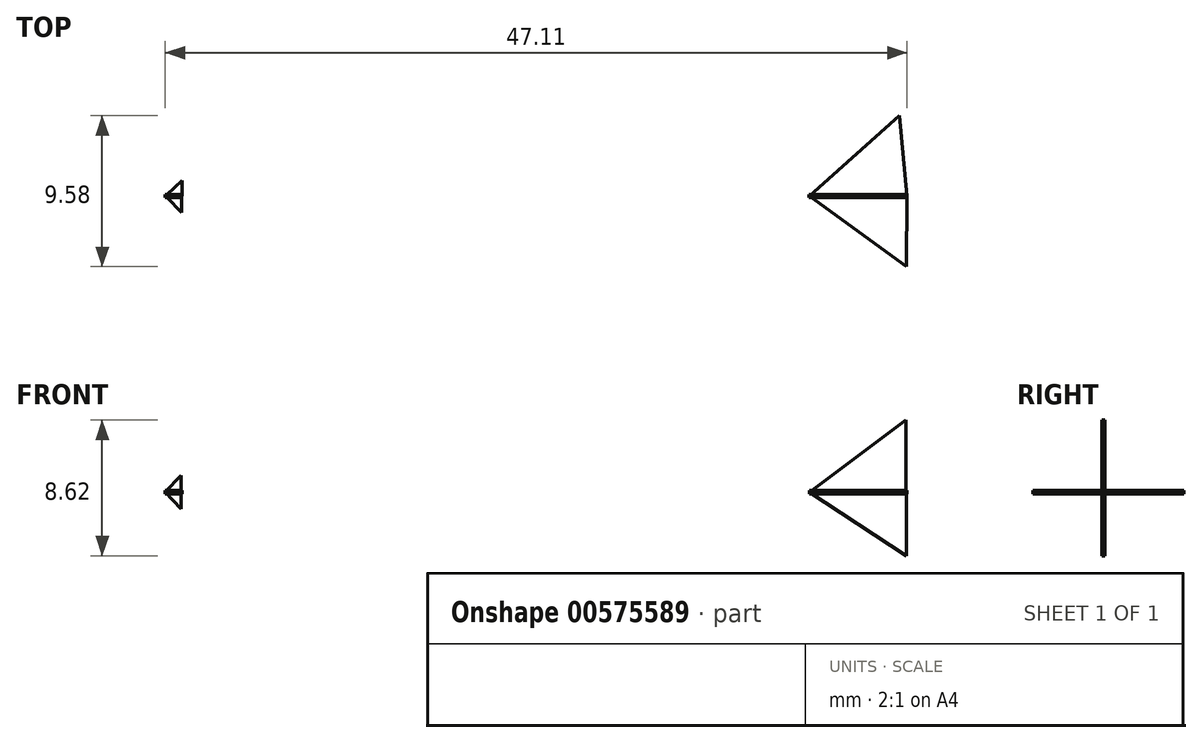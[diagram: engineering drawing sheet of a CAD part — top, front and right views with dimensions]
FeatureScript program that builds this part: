
annotation { "Feature Type Name" : "Feature", "Feature Type Description" : "" }
export const myFeature = defineFeature(function(context is Context, id is Id, definition is map)
    precondition{}
    {
        {
            var Q0;
            Q0=qCreatedBy(makeId("Front.planeOp"),FACE);
            var sketch = newSketch(context, id + "F0", { "sketchPlane" : qUnion([Q0])});
            skLineSegment(sketch, "E0", {"start": v(0, 67.82) * mm, "end": v(0, -67.31) * mm});
            skArc(sketch, "E1", {"start": v(0, 67.82) * mm, "mid": v(-28.44, 0.25) * mm, "end": v(0, -67.31) * mm});
            skSolve(sketch);
        }
        {
            var Q0;
            Q0=sQuery(id+"F0.wireOp",EDGE,"E1");
            extrude(context, id + "F1", {"bodyType" : ToolBodyType.SURFACE, "surfaceEntities" : qUnion([Q0]), "endBound" : BoundingType.SYMMETRIC, "depth" : 2.54 * mm, "offsetDistance" : 25.4 * mm});
        }
        {
            var Q0;
            Q0=qCreatedBy(makeId("Front.planeOp"),FACE);
            var sketch = newSketch(context, id + "F2", { "sketchPlane" : qUnion([Q0])});
            skLineSegment(sketch, "E2", {"start": v(-39.36, 0) * mm, "end": v(7.7, 0) * mm});
            skLineSegment(sketch, "E3", {"start": v(7.7, 0) * mm, "end": v(7.7, 4.58) * mm});
            skLineSegment(sketch, "E4", {"start": v(7.7, 4.58) * mm, "end": v(1.58, 0) * mm});
            skLineSegment(sketch, "E5", {"start": v(1.58, 0) * mm, "end": v(7.7, -4.6) * mm});
            skLineSegment(sketch, "E6", {"start": v(7.74, -4.6) * mm, "end": v(7.7, 0) * mm});
            skLineSegment(sketch, "E7", {"start": v(-39.36, 0) * mm, "end": v(-38.35, 1.07) * mm});
            skLineSegment(sketch, "E8", {"start": v(-38.35, 1.07) * mm, "end": v(-38.35, 0) * mm});
            skLineSegment(sketch, "E9", {"start": v(-38.35, 0) * mm, "end": v(-38.35, -1.06) * mm});
            skLineSegment(sketch, "E10", {"start": v(-38.35, -1.06) * mm, "end": v(-38.39, -1.06) * mm});
            skLineSegment(sketch, "E11", {"start": v(-39.36, 0) * mm, "end": v(-38.35, -1.06) * mm});
            skSolve(sketch);
        }
        {
            var Q0;
            Q0=qCreatedBy(makeId("Top.planeOp"),FACE);
            var sketch = newSketch(context, id + "F3", { "sketchPlane" : qUnion([Q0])});
            skPoint(sketch, "E12", {"position": v(-39.36, 0) * mm});
            skLineSegment(sketch, "E13", {"start": v(-39.36, 0) * mm, "end": v(-38.33, -1.04) * mm});
            skLineSegment(sketch, "E14", {"start": v(-39.36, 0) * mm, "end": v(-38.29, 1) * mm});
            skLineSegment(sketch, "E15", {"start": v(-38.29, 1) * mm, "end": v(-38.33, -1.04) * mm});
            skPoint(sketch, "E16", {"position": v(1.54, 0) * mm});
            skLineSegment(sketch, "E17", {"start": v(1.54, 0) * mm, "end": v(7.26, 5.1) * mm});
            skLineSegment(sketch, "E18", {"start": v(7.26, 5.1) * mm, "end": v(7.75, 0) * mm});
            skLineSegment(sketch, "E19", {"start": v(1.54, 0) * mm, "end": v(7.73, -4.48) * mm});
            skLineSegment(sketch, "E20", {"start": v(7.73, -4.48) * mm, "end": v(7.75, 0) * mm});
            skSolve(sketch);
        }
        {
            var Q0;
            {var subQ2=sQuery(id+"F2.wireOp",EDGE,"E9");Q0=makeQuery(id+"F2.imprint","IMPRINT",FACE,{"disambiguationData":[TD([[makeQuery(id+"F2.imprint","IMPRINT",EDGE,{"derivedFrom":subQ2}),-1.0]])]});}
            var Q1;
            {var subQ0=sQuery(id+"F2.wireOp",EDGE,"E7");Q1=makeQuery(id+"F2.imprint","IMPRINT",FACE,{"disambiguationData":[TD([[makeQuery(id+"F2.imprint","IMPRINT",EDGE,{"derivedFrom":subQ0}),-1.0]])]});}
            extrude(context, id + "F4", {"entities" : qUnion([Q0, Q1]), "endBound" : BoundingType.SYMMETRIC, "depth" : 0.2 * mm, "offsetDistance" : 25.4 * mm});
        }
        {
            var Q0;
            Q0=makeQuery(id+"F3.imprint","IMPRINT",FACE,{"disambiguationData":[TD([[makeQuery(id+"F3.imprint","IMPRINT",EDGE,{"derivedFrom":sQuery(id+"F3.wireOp",EDGE,"E13")}),1.0]])]});
            extrude(context, id + "F5", {"entities" : qUnion([Q0]), "operationType" : NewBodyOperationType.ADD, "endBound" : BoundingType.SYMMETRIC, "depth" : 0.2 * mm, "offsetDistance" : 25.4 * mm});
        }
        {
            var Q0;
            Q0 = qSketchRegion(id + "F3", true);
            extrude(context, id + "F6", {"entities" : qUnion([Q0]), "operationType" : NewBodyOperationType.ADD, "endBound" : BoundingType.SYMMETRIC, "depth" : 0.2 * mm, "offsetDistance" : 25.4 * mm});
        }
        {
            var Q0;
            Q0 = qSketchRegion(id + "F2", true);
            extrude(context, id + "F7", {"entities" : qUnion([Q0]), "endBound" : BoundingType.SYMMETRIC, "depth" : 0.2 * mm, "offsetDistance" : 25.4 * mm});
        }
        {
            var Q0;
            Q0=qCreatedBy(makeId("Front.planeOp"),FACE);
            var sketch = newSketch(context, id + "F8", { "sketchPlane" : qUnion([Q0])});
            skLineSegment(sketch, "E21", {"start": v(7.73, 0) * mm, "end": v(7.73, -4.09) * mm});
            skLineSegment(sketch, "E22", {"start": v(7.75, -4.06) * mm, "end": v(1.54, 0) * mm});
            skLineSegment(sketch, "E23", {"start": v(7.73, 0) * mm, "end": v(1.54, 0) * mm});
            skSolve(sketch);
        }
        {
            var Q0;
            {var subQ0=sQuery(id+"F8.wireOp",EDGE,"E23");Q0=makeQuery(id+"F8.imprint","IMPRINT",FACE,{"disambiguationData":[TD([[makeQuery(id+"F8.imprint","IMPRINT",EDGE,{"derivedFrom":subQ0}),1.0]])]});}
            extrude(context, id + "F9", {"entities" : qUnion([Q0]), "endBound" : BoundingType.SYMMETRIC, "depth" : 0.2 * mm, "offsetDistance" : 25.4 * mm});
        }
    });
